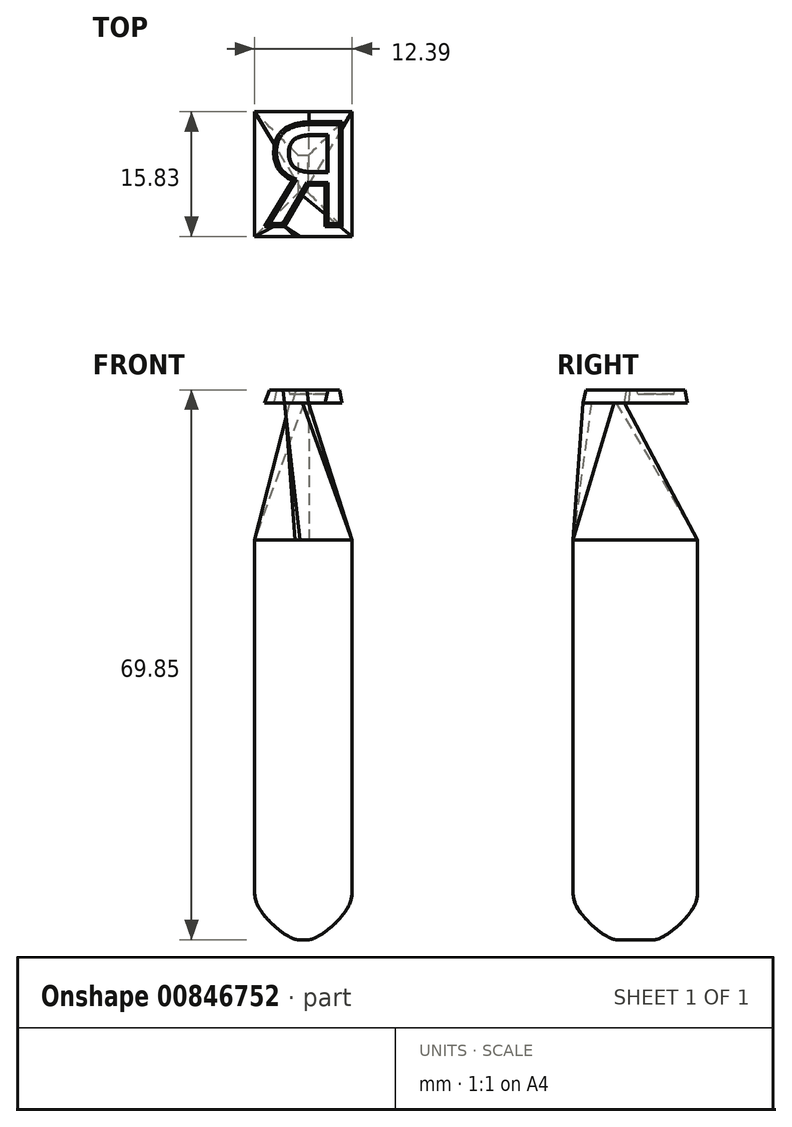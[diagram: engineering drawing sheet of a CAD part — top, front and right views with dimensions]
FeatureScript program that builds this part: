
annotation { "Feature Type Name" : "Feature", "Feature Type Description" : "" }
export const myFeature = defineFeature(function(context is Context, id is Id, definition is map)
    precondition{}
    {
        {
            var Q0;
            Q0=qCreatedBy(makeId("Top.planeOp"),FACE);
            var sketch = newSketch(context, id + "F0", { "sketchPlane" : qUnion([Q0])});
            skText(sketch, "E0", { "text": "R", "fontName": "OpenSans-Regular.ttf"});
            const initialGuessF0  = {"E0": [-0.01175, 0, 1, 0, 0.0127]};
            skSetInitialGuess(sketch, initialGuessF0);
            skSolve(sketch);
        }
        {
            var Q0;
            Q0 = qSketchRegion(id + "F0", true);
            extrude(context, id + "F1", {"entities" : qUnion([Q0]), "depth" : 1.65 * mm, "offsetDistance" : 25.4 * mm, "hasDraft" : true, "draftAngle" : 12 * degree});
        }
        {
            var Q0;
            Q0=qCreatedBy(makeId("Top.planeOp"),FACE);
            var sketch = newSketch(context, id + "F2", { "sketchPlane" : qUnion([Q0])});
            skLineSegment(sketch, "E1", {"start": v(0, 0) * mm, "end": v(0, 25.9) * mm, "construction": true});
            skSolve(sketch);
        }
        {
            var Q0;
            Q0=makeQuery(id+"F1.opExtrude","SWEPT_BODY",BODY,{"disambiguationData":[OSD([sQuery(id+"F0.wireOp",EDGE,"E0.sketch_text.stroke-0"),sQuery(id+"F0.wireOp",EDGE,"E0.sketch_text.stroke-1"),sQuery(id+"F0.wireOp",EDGE,"E0.sketch_text.stroke-2"),sQuery(id+"F0.wireOp",EDGE,"E0.sketch_text.stroke-3"),sQuery(id+"F0.wireOp",EDGE,"E0.sketch_text.stroke-4"),sQuery(id+"F0.wireOp",EDGE,"E0.sketch_text.stroke-5"),sQuery(id+"F0.wireOp",EDGE,"E0.sketch_text.stroke-6"),sQuery(id+"F0.wireOp",EDGE,"E0.sketch_text.stroke-7"),sQuery(id+"F0.wireOp",EDGE,"E0.sketch_text.stroke-8"),sQuery(id+"F0.wireOp",EDGE,"E0.sketch_text.stroke-9"),sQuery(id+"F0.wireOp",EDGE,"E0.sketch_text.stroke-10"),sQuery(id+"F0.wireOp",EDGE,"E0.sketch_text.stroke-11"),sQuery(id+"F0.wireOp",EDGE,"E0.sketch_text.stroke-12"),sQuery(id+"F0.wireOp",EDGE,"E0.sketch_text.stroke-13"),sQuery(id+"F0.wireOp",EDGE,"E0.sketch_text.stroke-14"),sQuery(id+"F0.wireOp",EDGE,"E0.sketch_text.stroke-15"),sQuery(id+"F0.wireOp",EDGE,"E0.sketch_text.stroke-16"),sQuery(id+"F0.wireOp",EDGE,"E0.sketch_text.stroke-17")])]});
            var Q1;
            Q1=sQuery(id+"F2.wireOp",EDGE,"E1");
            transform(context, id + "F3", {"entities" : qUnion([Q0]), "transformType" : TransformType.ROTATION, "transformAxis" : qUnion([Q1]), "angle" : 180 * degree, "makeCopy" : false});
        }
        {
            var Q0;
            Q0=qCreatedBy(makeId("Top.planeOp"),FACE);
            cPlane(context, id + "F4", {"entities" : qUnion([Q0]), "cplaneType" : CPlaneType.OFFSET, "offset" : 19.05 * mm, "oppositeDirection" : true, "width" : 152.4 * mm, "height" : 152.4 * mm});
        }
        {
            var Q0;
            Q0=qCreatedBy(id+"F4.planeOp",FACE);
            var sketch = newSketch(context, id + "F5", { "sketchPlane" : qUnion([Q0])});
            skLineSegment(sketch, "E2.bottom", {"start": v(-0.75, -1.62) * mm, "end": v(1.58, -1.62) * mm});
            skLineSegment(sketch, "E2.top", {"start": v(-0.75, 14.21) * mm, "end": v(11.64, 14.21) * mm});
            skLineSegment(sketch, "E2.left", {"start": v(-0.75, -1.62) * mm, "end": v(-0.75, 5.3) * mm});
            skLineSegment(sketch, "E2.right", {"start": v(11.64, -1.62) * mm, "end": v(11.64, 14.21) * mm});
            skLineSegment(sketch, "E3", {"start": v(1.58, -1.62) * mm, "end": v(3.23, -1.62) * mm});
            skLineSegment(sketch, "E4", {"start": v(3.23, -1.62) * mm, "end": v(6.34, -1.62) * mm});
            skLineSegment(sketch, "E5", {"start": v(6.34, -1.62) * mm, "end": v(9.8, -1.62) * mm});
            skLineSegment(sketch, "E6", {"start": v(9.8, -1.62) * mm, "end": v(11.64, -1.62) * mm});
            skLineSegment(sketch, "E7", {"start": v(-0.75, 5.3) * mm, "end": v(-0.75, 14.21) * mm});
            skSolve(sketch);
        }
        {
            var Q0;
            Q0=makeQuery(id+"F1.opExtrude","CAP_FACE",FACE,{"disambiguationData":[OSD([sQuery(id+"F0.wireOp",EDGE,"E0.sketch_text.stroke-0"),sQuery(id+"F0.wireOp",EDGE,"E0.sketch_text.stroke-1"),sQuery(id+"F0.wireOp",EDGE,"E0.sketch_text.stroke-2"),sQuery(id+"F0.wireOp",EDGE,"E0.sketch_text.stroke-3"),sQuery(id+"F0.wireOp",EDGE,"E0.sketch_text.stroke-4"),sQuery(id+"F0.wireOp",EDGE,"E0.sketch_text.stroke-5"),sQuery(id+"F0.wireOp",EDGE,"E0.sketch_text.stroke-6"),sQuery(id+"F0.wireOp",EDGE,"E0.sketch_text.stroke-7"),sQuery(id+"F0.wireOp",EDGE,"E0.sketch_text.stroke-8"),sQuery(id+"F0.wireOp",EDGE,"E0.sketch_text.stroke-9"),sQuery(id+"F0.wireOp",EDGE,"E0.sketch_text.stroke-10"),sQuery(id+"F0.wireOp",EDGE,"E0.sketch_text.stroke-11"),sQuery(id+"F0.wireOp",EDGE,"E0.sketch_text.stroke-12"),sQuery(id+"F0.wireOp",EDGE,"E0.sketch_text.stroke-13"),sQuery(id+"F0.wireOp",EDGE,"E0.sketch_text.stroke-14"),sQuery(id+"F0.wireOp",EDGE,"E0.sketch_text.stroke-15"),sQuery(id+"F0.wireOp",EDGE,"E0.sketch_text.stroke-16"),sQuery(id+"F0.wireOp",EDGE,"E0.sketch_text.stroke-17")])],"isStart":false});
            var sketch = newSketch(context, id + "F6", { "sketchPlane" : qUnion([Q0])});
            skLineSegment(sketch, "E8", {"start": v(8.97, -11.82) * mm, "end": v(4.86, -11.82) * mm});
            skLineSegment(sketch, "E9", {"start": v(4.86, -11.82) * mm, "end": v(2.73, -9.63) * mm});
            skLineSegment(sketch, "E10", {"start": v(2.73, -9.63) * mm, "end": v(3.12, -7.47) * mm});
            skLineSegment(sketch, "E11", {"start": v(3.12, -7.47) * mm, "end": v(5.2, -6.03) * mm});
            skLineSegment(sketch, "E12", {"start": v(5.2, -6.03) * mm, "end": v(8.61, -5.76) * mm});
            skLineSegment(sketch, "E13", {"start": v(8.61, -5.76) * mm, "end": v(9.54, -6.33) * mm});
            skLineSegment(sketch, "E14", {"start": v(9.54, -6.33) * mm, "end": v(8.97, -11.82) * mm});
            skSolve(sketch);
        }
        {
            var Q0;
            Q0 = qSketchRegion(id + "F6", true);
            extrude(context, id + "F7", {"entities" : qUnion([Q0]), "operationType" : NewBodyOperationType.ADD, "oppositeDirection" : true, "depth" : 1.14 * mm, "offsetDistance" : 25.4 * mm});
        }
        {
            var Q0;
            Q0=makeQuery(id+"F5.imprint","IMPRINT",FACE,{"disambiguationData":[TD([[makeQuery(id+"F5.imprint","IMPRINT",EDGE,{"derivedFrom":sQuery(id+"F5.wireOp",EDGE,"E2.bottom")}),1.0]])]});
            extrude(context, id + "F8", {"entities" : qUnion([Q0]), "operationType" : NewBodyOperationType.ADD, "oppositeDirection" : true, "depth" : 44.45 * mm, "offsetDistance" : 25.4 * mm});
        }
        {
            var Q0;
            Q0=makeQuery(id+"F7.boolean.opBoolean","MERGE",FACE,{"derivedFrom":[makeQuery(id+"F1.opExtrude","CAP_FACE",FACE,{"disambiguationData":[OSD([sQuery(id+"F0.wireOp",EDGE,"E0.sketch_text.stroke-0"),sQuery(id+"F0.wireOp",EDGE,"E0.sketch_text.stroke-1"),sQuery(id+"F0.wireOp",EDGE,"E0.sketch_text.stroke-2"),sQuery(id+"F0.wireOp",EDGE,"E0.sketch_text.stroke-3"),sQuery(id+"F0.wireOp",EDGE,"E0.sketch_text.stroke-4"),sQuery(id+"F0.wireOp",EDGE,"E0.sketch_text.stroke-5"),sQuery(id+"F0.wireOp",EDGE,"E0.sketch_text.stroke-6"),sQuery(id+"F0.wireOp",EDGE,"E0.sketch_text.stroke-7"),sQuery(id+"F0.wireOp",EDGE,"E0.sketch_text.stroke-8"),sQuery(id+"F0.wireOp",EDGE,"E0.sketch_text.stroke-9"),sQuery(id+"F0.wireOp",EDGE,"E0.sketch_text.stroke-10"),sQuery(id+"F0.wireOp",EDGE,"E0.sketch_text.stroke-11"),sQuery(id+"F0.wireOp",EDGE,"E0.sketch_text.stroke-12"),sQuery(id+"F0.wireOp",EDGE,"E0.sketch_text.stroke-13"),sQuery(id+"F0.wireOp",EDGE,"E0.sketch_text.stroke-14"),sQuery(id+"F0.wireOp",EDGE,"E0.sketch_text.stroke-15"),sQuery(id+"F0.wireOp",EDGE,"E0.sketch_text.stroke-16"),sQuery(id+"F0.wireOp",EDGE,"E0.sketch_text.stroke-17")])],"isStart":false}),makeQuery(id+"F7.opExtrude","CAP_FACE",FACE,{"disambiguationData":[OSD([sQuery(id+"F6.wireOp",EDGE,"E8"),sQuery(id+"F6.wireOp",EDGE,"E9"),sQuery(id+"F6.wireOp",EDGE,"E10"),sQuery(id+"F6.wireOp",EDGE,"E11"),sQuery(id+"F6.wireOp",EDGE,"E12"),sQuery(id+"F6.wireOp",EDGE,"E13"),sQuery(id+"F6.wireOp",EDGE,"E14")])],"isStart":true})]});
            var sketch = newSketch(context, id + "F9", { "sketchPlane" : qUnion([Q0])});
            skLineSegment(sketch, "E15.0.0", {"start": v(8.2, -4.89) * mm, "end": v(6.12, -4.89) * mm});
            skLineSegment(sketch, "E15.0.1", {"start": v(6.12, -4.89) * mm, "end": v(3.08, 0.35) * mm});
            skLineSegment(sketch, "E15.0.2", {"start": v(3.08, 0.35) * mm, "end": v(0.52, 0.35) * mm});
            skLineSegment(sketch, "E15.0.3", {"start": v(0.52, 0.35) * mm, "end": v(4.05, -5.48) * mm});
            skFitSpline(sketch, "E15.0.4", {"points": [v(4.22, -5.54) * mm, v(3.9, -5.67) * mm, v(3.6, -5.83) * mm, v(3, -6.23) * mm, v(2.7, -6.5) * mm, v(2.25, -7.1) * mm, v(2.08, -7.45) * mm, v(1.85, -8.2) * mm, v(1.8, -8.6) * mm, v(1.8, -9.03) * mm]});
            skFitSpline(sketch, "E15.0.5", {"points": [v(1.8, -9.03) * mm, v(1.8, -9.65) * mm, v(1.9, -10.2) * mm, v(2.3, -11.16) * mm, v(2.6, -11.57) * mm, v(3, -11.89) * mm]});
            skFitSpline(sketch, "E15.0.6", {"points": [v(3, -11.89) * mm, v(3.4, -12.2) * mm, v(3.9, -12.44) * mm, v(5.08, -12.75) * mm, v(5.77, -12.82) * mm, v(6.56, -12.82) * mm]});
            skLineSegment(sketch, "E15.0.7", {"start": v(6.56, -12.94) * mm, "end": v(10.37, -12.94) * mm});
            skLineSegment(sketch, "E15.0.8", {"start": v(10.37, -12.94) * mm, "end": v(10.37, 0.35) * mm});
            skLineSegment(sketch, "E15.0.9", {"start": v(10.37, 0.35) * mm, "end": v(8.2, 0.35) * mm});
            skLineSegment(sketch, "E15.0.10", {"start": v(8.2, 0.35) * mm, "end": v(8.2, -4.89) * mm});
            skSolve(sketch);
        }
        {
            var Q0;
            Q0=makeQuery(id+"F8.opExtrude","CAP_FACE",FACE,{"disambiguationData":[OSD([sQuery(id+"F5.wireOp",EDGE,"E2.bottom"),sQuery(id+"F5.wireOp",EDGE,"E2.top"),sQuery(id+"F5.wireOp",EDGE,"E2.left"),sQuery(id+"F5.wireOp",EDGE,"E2.right"),sQuery(id+"F5.wireOp",EDGE,"E3"),sQuery(id+"F5.wireOp",EDGE,"E4"),sQuery(id+"F5.wireOp",EDGE,"E5"),sQuery(id+"F5.wireOp",EDGE,"E6"),sQuery(id+"F5.wireOp",EDGE,"E7")])],"isStart":true});
            var sketch = newSketch(context, id + "F10", { "sketchPlane" : qUnion([Q0])});
            skLineSegment(sketch, "E16.0", {"start": v(-0.75, -1.62) * mm, "end": v(-0.75, 4.02) * mm});
            skLineSegment(sketch, "E17", {"start": v(6.17, 14.21) * mm, "end": v(11.64, 14.21) * mm});
            skLineSegment(sketch, "E18", {"start": v(6.17, 14.21) * mm, "end": v(-0.75, 14.21) * mm});
            skLineSegment(sketch, "E19", {"start": v(-0.75, 14.21) * mm, "end": v(-0.75, 9.33) * mm});
            skLineSegment(sketch, "E20", {"start": v(-0.75, 9.33) * mm, "end": v(-0.75, 4.02) * mm});
            skLineSegment(sketch, "E21", {"start": v(-0.75, -1.62) * mm, "end": v(4.41, -1.62) * mm});
            skLineSegment(sketch, "E22", {"start": v(4.41, -1.62) * mm, "end": v(5.05, -1.62) * mm});
            skLineSegment(sketch, "E23", {"start": v(5.05, -1.62) * mm, "end": v(6.22, -1.62) * mm});
            skLineSegment(sketch, "E24", {"start": v(6.22, -1.62) * mm, "end": v(7.72, -1.62) * mm});
            skLineSegment(sketch, "E25", {"start": v(7.72, -1.62) * mm, "end": v(11.64, -1.62) * mm});
            skSolve(sketch);
        }
        {
            var Q1;
            Q1=makeQuery(id+"F9.imprint","IMPRINT",FACE,{"disambiguationData":[TD([[makeQuery(id+"F9.imprint","IMPRINT",EDGE,{"derivedFrom":sQuery(id+"F9.wireOp",EDGE,"E15.0.0")}),-1.0]])]});
            var Q2;
            Q2=makeQuery(id+"F10.imprint","IMPRINT",FACE,{"disambiguationData":[TD([[makeQuery(id+"F10.imprint","IMPRINT",EDGE,{"derivedFrom":sQuery(id+"F10.wireOp",EDGE,"E16.0")}),-1.0]])]});
            var Q3;
            Q3=sQuery(id+"F10.wireOp",VERTEX,"E21.end");
            var Q4;
            Q4=sQuery(id+"F9.wireOp",VERTEX,"E15.0.1.end");
            loft(context, id + "F11", {"operationType" : NewBodyOperationType.ADD, "sheetProfilesArray" : [{ "sheetProfileEntities" : qUnion([Q1]) }, { "sheetProfileEntities" : qUnion([Q2]) }], "matchConnections" : true, "connections" : [{ "connectionEntities" : qUnion([Q3, Q4]), "connectionEdgeQueries" : qUnion([]), "connectionEdgeParameters" : [] }]});
        }
        {
            var Q0;
            Q0=makeQuery(id+"F8.opExtrude","CAP_FACE",FACE,{"disambiguationData":[OSD([sQuery(id+"F5.wireOp",EDGE,"E2.bottom"),sQuery(id+"F5.wireOp",EDGE,"E2.top"),sQuery(id+"F5.wireOp",EDGE,"E2.left"),sQuery(id+"F5.wireOp",EDGE,"E2.right"),sQuery(id+"F5.wireOp",EDGE,"E3"),sQuery(id+"F5.wireOp",EDGE,"E4"),sQuery(id+"F5.wireOp",EDGE,"E5"),sQuery(id+"F5.wireOp",EDGE,"E6"),sQuery(id+"F5.wireOp",EDGE,"E7")])],"isStart":false});
            cPlane(context, id + "F12", {"entities" : qUnion([Q0]), "cplaneType" : CPlaneType.OFFSET, "offset" : 6.35 * mm, "width" : 152.4 * mm, "height" : 152.4 * mm});
        }
        {
            var Q0;
            Q0=qCreatedBy(id+"F12.planeOp",FACE);
            var sketch = newSketch(context, id + "F13", { "sketchPlane" : qUnion([Q0])});
            skLineSegment(sketch, "E26.bottom", {"start": v(6.05, -3.97) * mm, "end": v(4.84, -3.97) * mm});
            skLineSegment(sketch, "E26.top", {"start": v(6.05, -8.63) * mm, "end": v(4.84, -8.63) * mm});
            skLineSegment(sketch, "E26.left", {"start": v(6.05, -3.97) * mm, "end": v(6.05, -8.63) * mm});
            skLineSegment(sketch, "E26.right", {"start": v(4.84, -3.97) * mm, "end": v(4.84, -8.63) * mm});
            skSolve(sketch);
        }
        {
            var Q1;
            Q1=makeQuery(id+"F8.opExtrude","CAP_FACE",FACE,{"disambiguationData":[OSD([sQuery(id+"F5.wireOp",EDGE,"E2.bottom"),sQuery(id+"F5.wireOp",EDGE,"E2.top"),sQuery(id+"F5.wireOp",EDGE,"E2.left"),sQuery(id+"F5.wireOp",EDGE,"E2.right"),sQuery(id+"F5.wireOp",EDGE,"E3"),sQuery(id+"F5.wireOp",EDGE,"E4"),sQuery(id+"F5.wireOp",EDGE,"E5"),sQuery(id+"F5.wireOp",EDGE,"E6"),sQuery(id+"F5.wireOp",EDGE,"E7")])],"isStart":false});
            var Q2;
            Q2=makeQuery(id+"F13.imprint","IMPRINT",FACE,{"disambiguationData":[TD([[makeQuery(id+"F13.imprint","IMPRINT",EDGE,{"derivedFrom":sQuery(id+"F13.wireOp",EDGE,"E26.bottom")}),1.0]])]});
            loft(context, id + "F14", {"operationType" : NewBodyOperationType.ADD, "startCondition" : LoftEndDerivativeType.MATCH_CURVATURE, "startMagnitude" : 1, "endCondition" : LoftEndDerivativeType.TANGENT_TO_PROFILE, "endMagnitude" : 1, "sheetProfilesArray" : [{ "sheetProfileEntities" : qUnion([Q1]) }, { "sheetProfileEntities" : qUnion([Q2]) }]});
        }
    });
